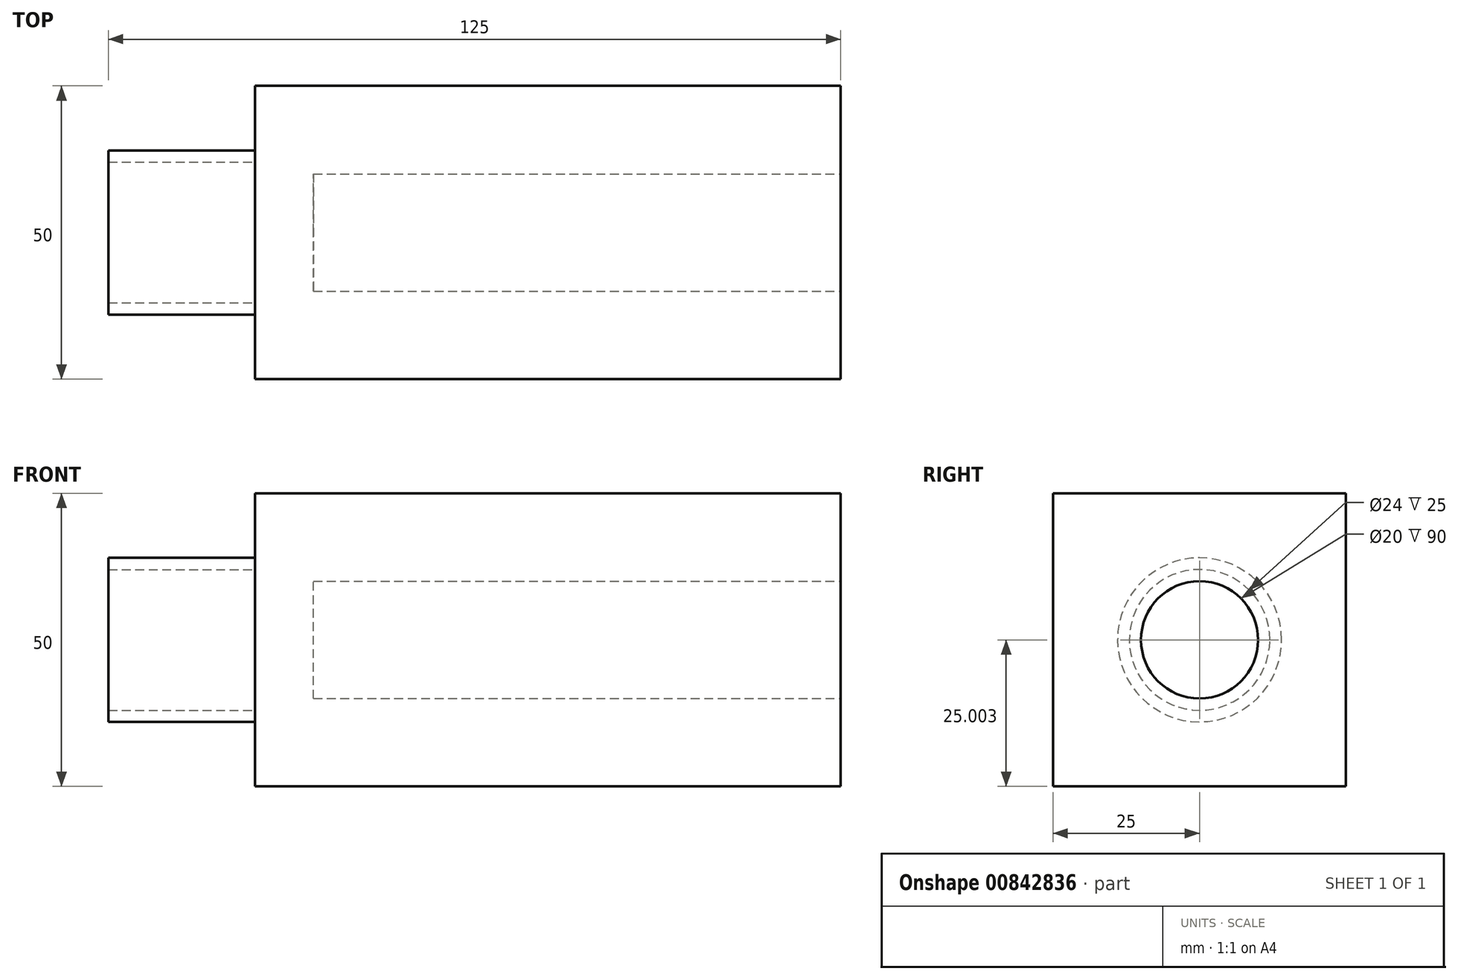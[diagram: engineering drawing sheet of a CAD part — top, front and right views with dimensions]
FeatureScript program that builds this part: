
annotation { "Feature Type Name" : "Feature", "Feature Type Description" : "" }
export const myFeature = defineFeature(function(context is Context, id is Id, definition is map)
    precondition{}
    {
        {
            var Q0;
            Q0=qCreatedBy(makeId("Front.planeOp"),FACE);
            var sketch = newSketch(context, id + "F0", { "sketchPlane" : qUnion([Q0])});
            skLineSegment(sketch, "E0.bottom", {"start": v(5.65, 22.32) * mm, "end": v(105.65, 22.32) * mm});
            skLineSegment(sketch, "E0.top", {"start": v(5.65, -27.68) * mm, "end": v(105.65, -27.68) * mm});
            skLineSegment(sketch, "E0.left", {"start": v(5.65, 22.32) * mm, "end": v(5.65, -27.68) * mm});
            skLineSegment(sketch, "E0.right", {"start": v(105.65, 22.32) * mm, "end": v(105.65, -27.68) * mm});
            skSolve(sketch);
        }
        {
            var Q0;
            Q0=makeQuery(id+"F0.imprint","IMPRINT",FACE,{"disambiguationData":[TD([[makeQuery(id+"F0.imprint","IMPRINT",EDGE,{"derivedFrom":sQuery(id+"F0.wireOp",EDGE,"E0.bottom")}),-1.0]])]});
            extrude(context, id + "F1", {"entities" : qUnion([Q0]), "depth" : 50 * mm, "offsetDistance" : 25 * mm});
        }
        {
            var Q0;
            Q0=makeQuery(id+"F1.opExtrude","SWEPT_FACE",FACE,{"disambiguationData":[OSD([sQuery(id+"F0.wireOp",EDGE,"E0.left")])]});
            var sketch = newSketch(context, id + "F2", { "sketchPlane" : qUnion([Q0])});
            skCircle(sketch, "E1", {"center": v(25, -2.68) * mm, "radius": 12 * mm});
            skCircle(sketch, "E2", {"center": v(25, -2.68) * mm, "radius": 14 * mm});
            skSolve(sketch);
        }
        {
            var Q0;
            Q0=makeQuery(id+"F2.imprint","IMPRINT",FACE,{"disambiguationData":[TD([[makeQuery(id+"F2.imprint","IMPRINT",EDGE,{"derivedFrom":sQuery(id+"F2.wireOp",EDGE,"E1")}),-1.0]])]});
            extrude(context, id + "F3", {"entities" : qUnion([Q0]), "operationType" : NewBodyOperationType.ADD, "depth" : 25 * mm, "offsetDistance" : 25 * mm});
        }
        {
            var Q0;
            Q0=makeQuery(id+"F1.opExtrude","SWEPT_FACE",FACE,{"disambiguationData":[OSD([sQuery(id+"F0.wireOp",EDGE,"E0.right")])]});
            var sketch = newSketch(context, id + "F4", { "sketchPlane" : qUnion([Q0])});
            skCircle(sketch, "E3", {"center": v(-25, -2.68) * mm, "radius": 10 * mm});
            skSolve(sketch);
        }
        {
            var Q0;
            Q0=makeQuery(id+"F4.imprint","IMPRINT",FACE,{"disambiguationData":[TD([[makeQuery(id+"F4.imprint","IMPRINT",EDGE,{"derivedFrom":sQuery(id+"F4.wireOp",EDGE,"E3")}),1.0]])]});
            extrude(context, id + "F5", {"entities" : qUnion([Q0]), "operationType" : NewBodyOperationType.REMOVE, "oppositeDirection" : true, "depth" : 90 * mm, "offsetDistance" : 25 * mm});
        }
    });
